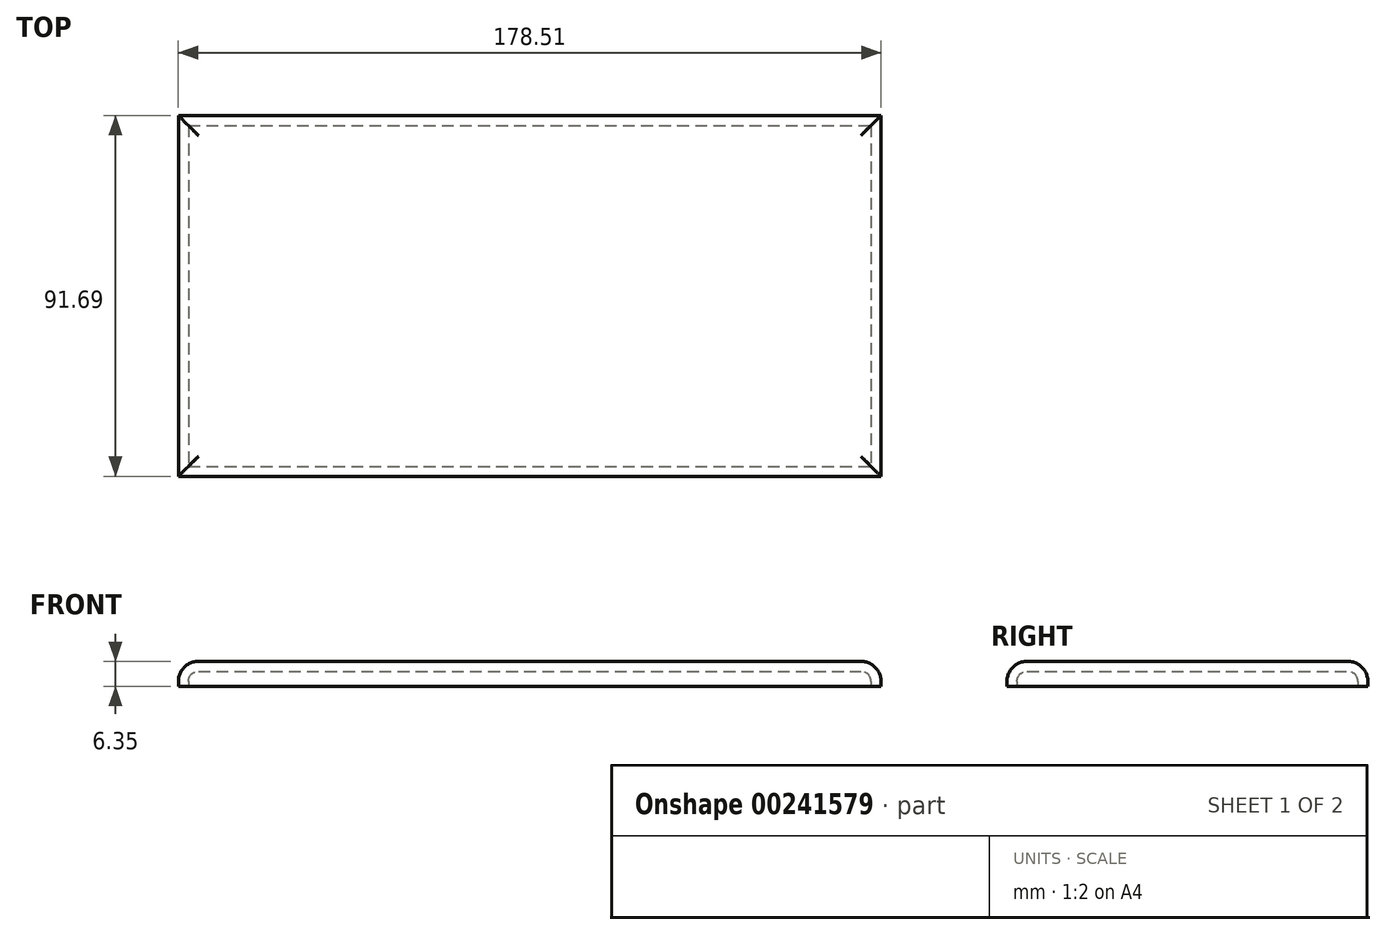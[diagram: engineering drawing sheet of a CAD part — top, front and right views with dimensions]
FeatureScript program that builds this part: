
annotation { "Feature Type Name" : "Feature", "Feature Type Description" : "" }
export const myFeature = defineFeature(function(context is Context, id is Id, definition is map)
    precondition{}
    {
        {
            var Q0;
            Q0=qCreatedBy(makeId("Top.planeOp"),FACE);
            var sketch = newSketch(context, id + "F0", { "sketchPlane" : qUnion([Q0])});
            skLineSegment(sketch, "E0.bottom", {"start": v(-120.18, 41.76) * mm, "end": v(58.33, 41.76) * mm});
            skLineSegment(sketch, "E0.top", {"start": v(-120.18, -49.93) * mm, "end": v(58.33, -49.93) * mm});
            skLineSegment(sketch, "E0.left", {"start": v(-120.18, 41.76) * mm, "end": v(-120.18, -49.93) * mm});
            skLineSegment(sketch, "E0.right", {"start": v(58.33, 41.76) * mm, "end": v(58.33, -49.93) * mm});
            skSolve(sketch);
        }
        {
            var Q0;
            Q0=makeQuery(id+"F0.imprint","IMPRINT",FACE,{"disambiguationData":[TD([[makeQuery(id+"F0.imprint","IMPRINT",EDGE,{"derivedFrom":sQuery(id+"F0.wireOp",EDGE,"E0.bottom")}),-1.0]])]});
            extrude(context, id + "F1", {"entities" : qUnion([Q0]), "depth" : 6.35 * mm});
        }
        {
            var Q0;
            Q0=makeQuery(id+"F1.opExtrude","CAP_EDGE",EDGE,{"disambiguationData":[OSD([sQuery(id+"F0.wireOp",EDGE,"E0.top")])],"isStart":false});
            var Q1;
            Q1=makeQuery(id+"F1.opExtrude","CAP_FACE",FACE,{"disambiguationData":[OSD([sQuery(id+"F0.wireOp",EDGE,"E0.bottom"),sQuery(id+"F0.wireOp",EDGE,"E0.top"),sQuery(id+"F0.wireOp",EDGE,"E0.left"),sQuery(id+"F0.wireOp",EDGE,"E0.right")])],"isStart":false});
            fillet(context, id + "F2", {"entities" : qUnion([Q0, Q1]), "radius" : 5.08 * mm, "tangentPropagation" : true, "allowEdgeOverflow" : false});
        }
        {
            var Q0;
            Q0=makeQuery(id+"F1.opExtrude","CAP_FACE",FACE,{"disambiguationData":[OSD([sQuery(id+"F0.wireOp",EDGE,"E0.bottom"),sQuery(id+"F0.wireOp",EDGE,"E0.top"),sQuery(id+"F0.wireOp",EDGE,"E0.left"),sQuery(id+"F0.wireOp",EDGE,"E0.right")])],"isStart":true});
            shell(context, id + "F3", {"entities" : qUnion([Q0]), "thickness" : 2.54 * mm});
        }
    });
